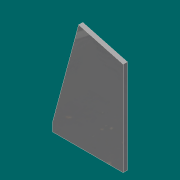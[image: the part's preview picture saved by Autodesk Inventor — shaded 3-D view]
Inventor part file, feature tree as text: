
AUTODESK INVENTOR PART (.ipt)
format: ipt  version: 2017 (Build 210142000, 142)  size: 75,264 bytes
history: native  units: in
note: dims shown in document units (in); Inventor stores cm internally (conversion verified against a paired STEP export)
features: extrude x1, sketch x1
ambient origin geometry x8: Origin, YZ Plane, XZ Plane, XY Plane, X Axis, Y Axis, Z Axis, Center Point
bodies: Solid1 (feature_tree)
feature tree (2):
  extrude  "Extrusion1"  Depth=0.25in
  sketch  "Sketch1"  dims[d0=2.0in d1=0.25in d2=15.0deg d3=3.0in d4=0.12in d5=0.0in]
